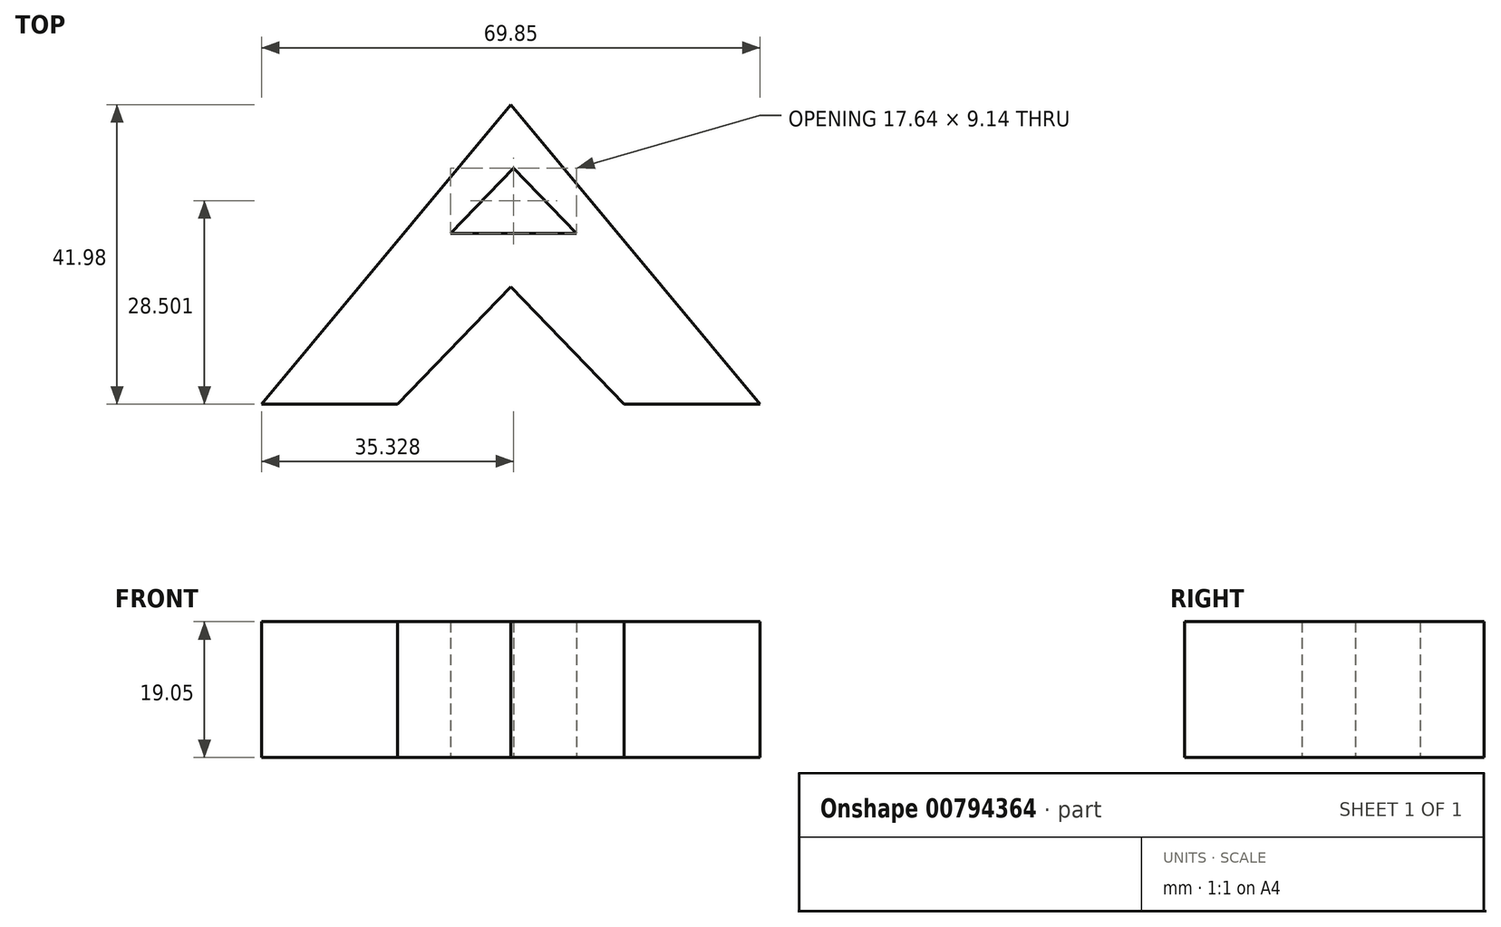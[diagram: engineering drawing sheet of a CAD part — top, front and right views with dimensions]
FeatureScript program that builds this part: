
annotation { "Feature Type Name" : "Feature", "Feature Type Description" : "" }
export const myFeature = defineFeature(function(context is Context, id is Id, definition is map)
    precondition{}
    {
        {
            var Q0;
            Q0=qCreatedBy(makeId("Top.planeOp"),FACE);
            var sketch = newSketch(context, id + "F0", { "sketchPlane" : qUnion([Q0])});
            skLineSegment(sketch, "E0", {"start": v(-44.15, -28.8) * mm, "end": v(-25.1, -28.8) * mm});
            skLineSegment(sketch, "E1", {"start": v(-25.1, -28.8) * mm, "end": v(-9.22, -12.35) * mm});
            skLineSegment(sketch, "E2", {"start": v(-9.22, -12.35) * mm, "end": v(6.65, -28.8) * mm});
            skLineSegment(sketch, "E3", {"start": v(6.65, -28.8) * mm, "end": v(25.7, -28.8) * mm});
            skLineSegment(sketch, "E4", {"start": v(-25.1, -28.8) * mm, "end": v(6.65, -28.8) * mm});
            skLineSegment(sketch, "E5", {"start": v(-44.15, -28.8) * mm, "end": v(-9.22, 13.18) * mm});
            skLineSegment(sketch, "E6", {"start": v(-9.22, 13.18) * mm, "end": v(25.7, -28.8) * mm});
            skLineSegment(sketch, "E7", {"start": v(-8.82, 4.27) * mm, "end": v(0, -4.87) * mm});
            skLineSegment(sketch, "E8", {"start": v(-17.64, -4.87) * mm, "end": v(0, -4.87) * mm});
            skLineSegment(sketch, "E9", {"start": v(-8.82, 4.27) * mm, "end": v(-17.64, -4.87) * mm});
            skSolve(sketch);
        }
        {
            var Q0;
            Q0=makeQuery(id+"F0.imprint","IMPRINT",FACE,{"disambiguationData":[TD([[makeQuery(id+"F0.imprint","IMPRINT",EDGE,{"derivedFrom":sQuery(id+"F0.wireOp",EDGE,"E0")}),1.0]])]});
            extrude(context, id + "F1", {"entities" : qUnion([Q0]), "depth" : 19.05 * mm, "offsetDistance" : 25.4 * mm});
        }
    });
